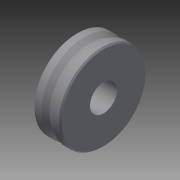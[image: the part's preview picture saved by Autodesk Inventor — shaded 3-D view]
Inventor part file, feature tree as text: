
AUTODESK INVENTOR PART (.ipt)
format: ipt  version: 2013 (Build 170138000, 138)  size: 101,888 bytes
history: native  units: mm
features: revolve x1, chamfer x1, sketch x1
ambient origin geometry x8: Origin, YZ Plane, XZ Plane, XY Plane, X Axis, Y Axis, Z Axis, Center Point
bodies: Solid1 (feature_tree)
feature tree (3):
  revolve  "Revolution1"  [1 undecoded]
  chamfer  "Chamfer1"  Distance=7.5mm
  sketch  "Sketch1"  dims[d0=2.5mm d1=8.0mm d2=7.5mm d3=2.0mm d4=5.0mm d5=90.0deg d6=0.25mm d7=2.0mm d8=45.0deg]
note: 1 required parameter value undecoded (feature->parameter linkage not recoverable at this tier; creation-order binding heuristic only, values carry confidence <= 0.55)
